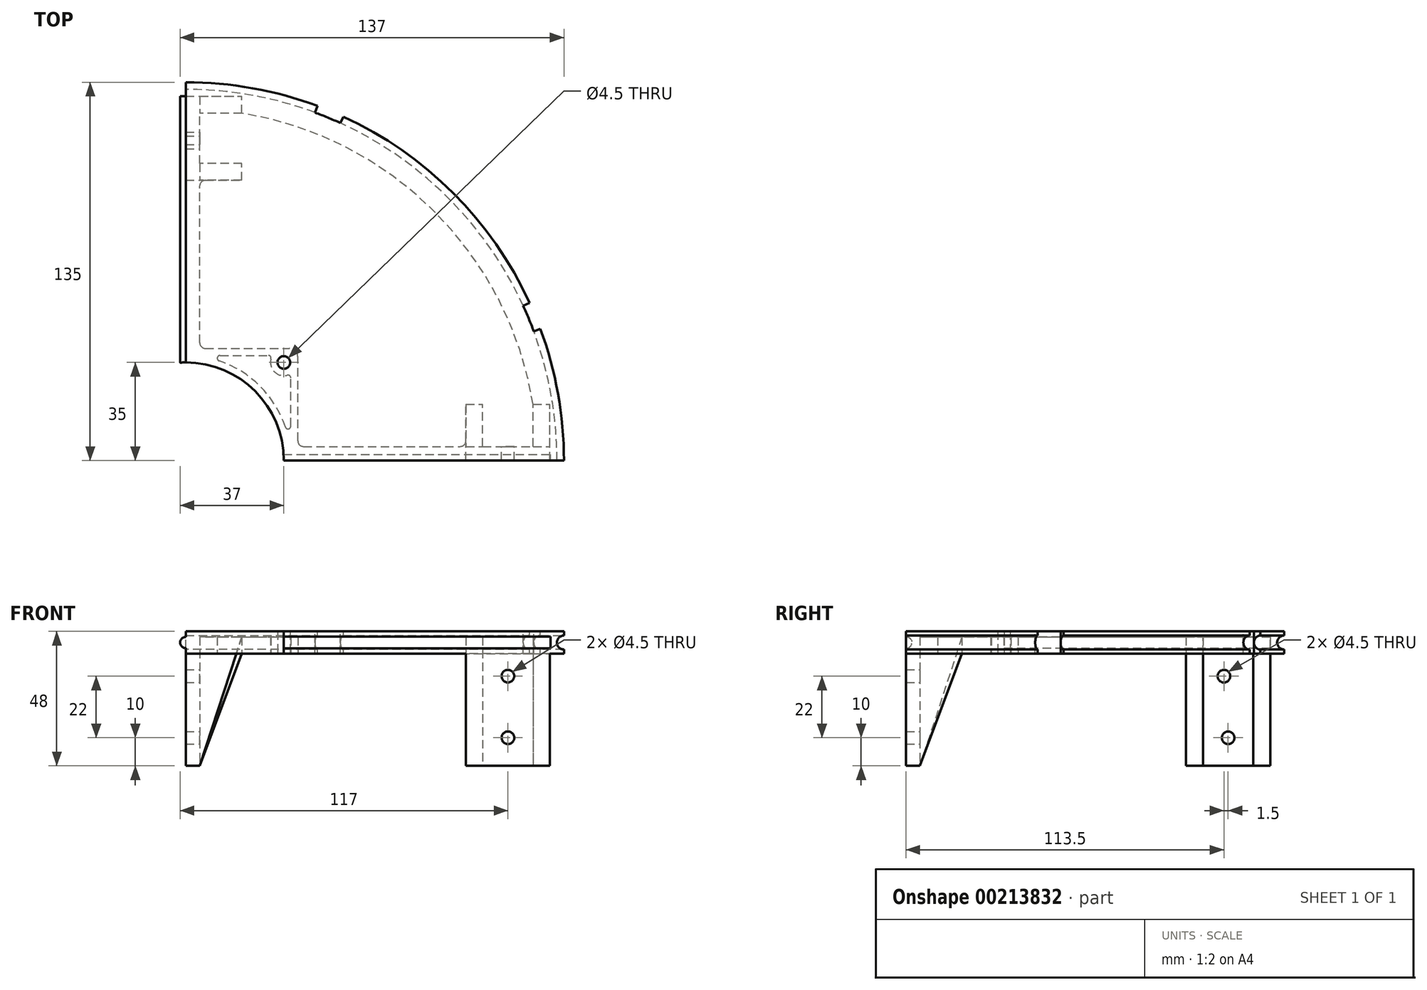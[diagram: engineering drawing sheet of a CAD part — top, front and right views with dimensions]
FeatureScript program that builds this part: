
annotation { "Feature Type Name" : "Feature", "Feature Type Description" : "" }
export const myFeature = defineFeature(function(context is Context, id is Id, definition is map)
    precondition{}
    {
        {
            var Q0;
            Q0=qCreatedBy(makeId("Top.planeOp"),FACE);
            var sketch = newSketch(context, id + "F0", { "sketchPlane" : qUnion([Q0])});
            skArc(sketch, "E0", {"start": v(135, 0) * mm, "mid": v(95.46, 95.46) * mm, "end": v(0, 135) * mm});
            skArc(sketch, "E1", {"start": v(35, 0) * mm, "mid": v(24.75, 24.75) * mm, "end": v(0, 35) * mm});
            skLineSegment(sketch, "E2.trimOffspring", {"start": v(35, 0) * mm, "end": v(135, 0) * mm});
            skLineSegment(sketch, "E3.1.5", {"start": v(0, 35) * mm, "end": v(0, 135) * mm});
            skCircle(sketch, "E4", {"center": v(35, 35) * mm, "radius": 2.25 * mm});
            skSolve(sketch);
        }
        {
            var Q0;
            Q0=qSketchRegion(id+"F0",true);
            extrude(context, id + "F1", {"entities" : qUnion([Q0]), "depth" : 8 * mm});
        }
        {
            var Q0;
            Q0=qCreatedBy(makeId("Top.planeOp"),FACE);
            cPlane(context, id + "F2", {"entities" : qUnion([Q0]), "cplaneType" : CPlaneType.OFFSET, "offset" : 4 * mm, "width" : 150 * mm, "height" : 150 * mm});
        }
        {
            var Q0;
            Q0=qCreatedBy(id+"F2.planeOp",FACE);
            var sketch = newSketch(context, id + "F3", { "sketchPlane" : qUnion([Q0])});
            skCircle(sketch, "E5", {"center": v(0, 0) * mm, "radius": 135 * mm});
            skSolve(sketch);
        }
        {
            var Q0;
            Q0=makeQuery(id+"F1.opExtrude","SWEPT_FACE",FACE,{"disambiguationData":[OSD([sQuery(id+"F0.wireOp",EDGE,"E2.trimOffspring")])]});
            var sketch = newSketch(context, id + "F4", { "sketchPlane" : qUnion([Q0])});
            skCircle(sketch, "E6", {"center": v(135, 4) * mm, "radius": 2.5 * mm});
            skSolve(sketch);
        }
        {
            var Q0;
            Q0=qSketchRegion(id+"F4",true);
            var Q1;
            Q1=qConstructionFilter(qBodyType(qCreatedBy(id+"F3",EDGE),BodyType.WIRE),ConstructionObject.NO);
            sweep(context, id + "F5", {"operationType" : NewBodyOperationType.REMOVE, "profiles" : qUnion([Q0]), "path" : qUnion([Q1])});
        }
        {
            var Q0;
            Q0=makeQuery(id+"F1.opExtrude","CAP_FACE",FACE,{"disambiguationData":[OSD([sQuery(id+"F0.wireOp",EDGE,"E0"),sQuery(id+"F0.wireOp",EDGE,"E1"),sQuery(id+"F0.wireOp",EDGE,"E2.trimOffspring"),sQuery(id+"F0.wireOp",EDGE,"E3.1.5"),sQuery(id+"F0.wireOp",EDGE,"E4")])],"isStart":true});
            var sketch = newSketch(context, id + "F6", { "sketchPlane" : qUnion([Q0])});
            skLineSegment(sketch, "E7.bottom", {"start": v(100, 0) * mm, "end": v(130, 0) * mm});
            skLineSegment(sketch, "E7.top", {"start": v(100, -20) * mm, "end": v(130, -20) * mm});
            skLineSegment(sketch, "E7.left", {"start": v(100, 0) * mm, "end": v(100, -20) * mm});
            skLineSegment(sketch, "E7.right", {"start": v(130, 0) * mm, "end": v(130, -20) * mm});
            skLineSegment(sketch, "E8.bottom", {"start": v(0, -100) * mm, "end": v(20, -100) * mm});
            skLineSegment(sketch, "E8.top", {"start": v(0, -130) * mm, "end": v(20, -130) * mm});
            skLineSegment(sketch, "E8.left", {"start": v(0, -100) * mm, "end": v(0, -130) * mm});
            skLineSegment(sketch, "E8.right", {"start": v(20, -100) * mm, "end": v(20, -130) * mm});
            skSolve(sketch);
        }
        {
            var Q0;
            Q0=qSketchRegion(id+"F6",true);
            extrude(context, id + "F7", {"entities" : qUnion([Q0]), "operationType" : NewBodyOperationType.ADD, "depth" : 40 * mm});
        }
        {
            var Q0;
            Q0=makeQuery(id+"F7.opExtrude","CAP_FACE",FACE,{"disambiguationData":[OSD([sQuery(id+"F6.wireOp",EDGE,"E7.bottom"),sQuery(id+"F6.wireOp",EDGE,"E7.top"),sQuery(id+"F6.wireOp",EDGE,"E7.left"),sQuery(id+"F6.wireOp",EDGE,"E7.right")])],"isStart":false});
            var sketch = newSketch(context, id + "F8", { "sketchPlane" : qUnion([Q0])});
            skLineSegment(sketch, "E9.bottom", {"start": v(106, -5) * mm, "end": v(124, -5) * mm});
            skLineSegment(sketch, "E9.top", {"start": v(106, -20) * mm, "end": v(124, -20) * mm});
            skLineSegment(sketch, "E9.left", {"start": v(106, -5) * mm, "end": v(106, -20) * mm});
            skLineSegment(sketch, "E9.right", {"start": v(124, -5) * mm, "end": v(124, -20) * mm});
            skLineSegment(sketch, "E10.bottom", {"start": v(20, -106) * mm, "end": v(5, -106) * mm});
            skLineSegment(sketch, "E10.top", {"start": v(20, -124) * mm, "end": v(5, -124) * mm});
            skLineSegment(sketch, "E10.left", {"start": v(20, -106) * mm, "end": v(20, -124) * mm});
            skLineSegment(sketch, "E10.right", {"start": v(5, -106) * mm, "end": v(5, -124) * mm});
            skSolve(sketch);
        }
        {
            var Q0;
            Q0=qSketchRegion(id+"F8",true);
            extrude(context, id + "F9", {"entities" : qUnion([Q0]), "operationType" : NewBodyOperationType.REMOVE, "oppositeDirection" : true, "depth" : 40 * mm});
        }
        {
            var Q0;
            {var subQ0=sQuery(id+"F6.wireOp",EDGE,"E7.right");var subQ1=sQuery(id+"F6.wireOp",EDGE,"E7.top");Q0=makeQuery(id+"F9.boolean.opBoolean","SPLIT",EDGE,{"disambiguationData":[TD([makeQuery(id+"F7.opExtrude","SWEPT_FACE",FACE,{"disambiguationData":[OSD([subQ0])]})])],"derivedFrom":makeQuery(id+"F7.opExtrude","CAP_EDGE",EDGE,{"disambiguationData":[OSD([subQ1])],"isStart":false})});}
            chamfer(context, id + "F10", {"entities" : qUnion([Q0]), "chamferType" : ChamferType.TWO_OFFSETS, "width1" : 15 * mm, "oppositeDirection" : false, "width2" : 40 * mm, "tangentPropagation" : true});
        }
        {
            var Q0;
            Q0=makeQuery(id+"F9.boolean.opBoolean","COPY",FACE,{"derivedFrom":makeQuery(id+"F9.opExtrude","SWEPT_FACE",FACE,{"disambiguationData":[OSD([sQuery(id+"F8.wireOp",EDGE,"E9.bottom")])]})});
            var sketch = newSketch(context, id + "F11", { "sketchPlane" : qUnion([Q0])});
            skCircle(sketch, "E11", {"center": v(-115, -8) * mm, "radius": 2.25 * mm});
            skCircle(sketch, "E12", {"center": v(-115, -30) * mm, "radius": 2.25 * mm});
            skSolve(sketch);
        }
        {
            var Q0;
            Q0=qSketchRegion(id+"F11",true);
            extrude(context, id + "F12", {"entities" : qUnion([Q0]), "operationType" : NewBodyOperationType.REMOVE, "oppositeDirection" : true, "depth" : 25 * mm});
        }
        {
            var Q0;
            {var subQ0=sQuery(id+"F6.wireOp",EDGE,"E8.right");var subQ1=sQuery(id+"F6.wireOp",EDGE,"E8.top");Q0=makeQuery(id+"F9.boolean.opBoolean","SPLIT",EDGE,{"disambiguationData":[TD([makeQuery(id+"F7.opExtrude","SWEPT_FACE",FACE,{"disambiguationData":[OSD([subQ1])]})])],"derivedFrom":makeQuery(id+"F7.opExtrude","CAP_EDGE",EDGE,{"disambiguationData":[OSD([subQ0])],"isStart":false})});}
            chamfer(context, id + "F13", {"entities" : qUnion([Q0]), "chamferType" : ChamferType.TWO_OFFSETS, "width1" : 40 * mm, "oppositeDirection" : false, "width2" : 15 * mm, "tangentPropagation" : true});
        }
        {
            var Q0;
            Q0=makeQuery(id+"F9.boolean.opBoolean","COPY",FACE,{"derivedFrom":makeQuery(id+"F9.opExtrude","SWEPT_FACE",FACE,{"disambiguationData":[OSD([sQuery(id+"F8.wireOp",EDGE,"E10.right")])]})});
            var sketch = newSketch(context, id + "F14", { "sketchPlane" : qUnion([Q0])});
            skCircle(sketch, "E13", {"center": v(115, -30) * mm, "radius": 2.25 * mm});
            skCircle(sketch, "E14", {"center": v(113.5, -8) * mm, "radius": 2.25 * mm});
            skSolve(sketch);
        }
        {
            var Q0;
            Q0=qSketchRegion(id+"F14",true);
            extrude(context, id + "F15", {"entities" : qUnion([Q0]), "operationType" : NewBodyOperationType.REMOVE, "oppositeDirection" : true, "depth" : 25 * mm});
        }
        {
            var Q0;
            Q0=makeQuery(id+"F1.opExtrude","CAP_FACE",FACE,{"disambiguationData":[OSD([sQuery(id+"F0.wireOp",EDGE,"E0"),sQuery(id+"F0.wireOp",EDGE,"E1"),sQuery(id+"F0.wireOp",EDGE,"E2.trimOffspring"),sQuery(id+"F0.wireOp",EDGE,"E3.1.5"),sQuery(id+"F0.wireOp",EDGE,"E4")])],"isStart":false});
            var sketch = newSketch(context, id + "F16", { "sketchPlane" : qUnion([Q0])});
            skArc(sketch, "E15", {"start": v(124.2, 46.14) * mm, "mid": v(122.41, 50.71) * mm, "end": v(120.45, 55.2) * mm});
            skArc(sketch, "E16", {"start": v(126.55, 47.01) * mm, "mid": v(124.72, 51.67) * mm, "end": v(122.72, 56.25) * mm});
            skLineSegment(sketch, "E17", {"start": v(0, 0) * mm, "end": v(124.72, 51.66) * mm, "construction": true});
            skLineSegment(sketch, "E18", {"start": v(0, 0) * mm, "end": v(51.66, 124.72) * mm, "construction": true});
            skLineSegment(sketch, "E19", {"start": v(46.13, 124.21) * mm, "end": v(47, 126.55) * mm});
            skLineSegment(sketch, "E20", {"start": v(124.2, 46.14) * mm, "end": v(126.55, 47.01) * mm});
            skLineSegment(sketch, "E21", {"start": v(55.2, 120.45) * mm, "end": v(56.24, 122.73) * mm});
            skLineSegment(sketch, "E22", {"start": v(120.45, 55.2) * mm, "end": v(122.72, 56.25) * mm});
            skArc(sketch, "E23.trimOffspring", {"start": v(56.24, 122.73) * mm, "mid": v(51.66, 124.73) * mm, "end": v(47, 126.55) * mm});
            skArc(sketch, "E24.trimOffspring", {"start": v(55.2, 120.45) * mm, "mid": v(50.7, 122.42) * mm, "end": v(46.13, 124.21) * mm});
            skSolve(sketch);
        }
        {
            var Q0;
            Q0=qSketchRegion(id+"F16",true);
            extrude(context, id + "F17", {"entities" : qUnion([Q0]), "operationType" : NewBodyOperationType.REMOVE, "oppositeDirection" : true, "depth" : 25 * mm});
        }
        {
            var Q0;
            Q0=makeQuery(id+"F7.boolean.opBoolean","MERGE",FACE,{"derivedFrom":[makeQuery(id+"F1.opExtrude","SWEPT_FACE",FACE,{"disambiguationData":[OSD([sQuery(id+"F0.wireOp",EDGE,"E2.trimOffspring")])]}),makeQuery(id+"F7.opExtrude","SWEPT_FACE",FACE,{"disambiguationData":[OSD([sQuery(id+"F6.wireOp",EDGE,"E7.bottom")])]})]});
            var sketch = newSketch(context, id + "F18", { "sketchPlane" : qUnion([Q0])});
            skLineSegment(sketch, "E25", {"start": v(0, 4) * mm, "end": v(130.2, 4) * mm});
            skSolve(sketch);
        }
        {
            var Q0;
            Q0=makeQuery(id+"F7.boolean.opBoolean","MERGE",FACE,{"derivedFrom":[makeQuery(id+"F1.opExtrude","SWEPT_FACE",FACE,{"disambiguationData":[OSD([sQuery(id+"F0.wireOp",EDGE,"E3.1.5")])]}),makeQuery(id+"F7.opExtrude","SWEPT_FACE",FACE,{"disambiguationData":[OSD([sQuery(id+"F6.wireOp",EDGE,"E8.left")])]})]});
            var sketch = newSketch(context, id + "F19", { "sketchPlane" : qUnion([Q0])});
            skLineSegment(sketch, "E26", {"start": v(-130, 4) * mm, "end": v(0, 4) * mm});
            skSolve(sketch);
        }
        {
            var Q0;
            Q0=qCreatedBy(makeId("Front.planeOp"),FACE);
            var sketch = newSketch(context, id + "F20", { "sketchPlane" : qUnion([Q0])});
            skCircle(sketch, "E27", {"center": v(0, 4) * mm, "radius": 2 * mm});
            skSolve(sketch);
        }
        {
            var Q0;
            Q0=makeQuery(id+"F20.imprint","IMPRINT",FACE,{"disambiguationData":[TD([[makeQuery(id+"F20.imprint","IMPRINT",EDGE,{"derivedFrom":sQuery(id+"F20.wireOp",EDGE,"E27")}),1.0]])]});
            var Q1;
            Q1=sQuery(id+"F19.wireOp",EDGE,"E26");
            sweep(context, id + "F21", {"operationType" : NewBodyOperationType.ADD, "profiles" : qUnion([Q0]), "path" : qUnion([Q1])});
        }
        {
            var Q0;
            Q0=makeQuery(id+"F1.opExtrude","CAP_FACE",FACE,{"disambiguationData":[OSD([sQuery(id+"F0.wireOp",EDGE,"E0"),sQuery(id+"F0.wireOp",EDGE,"E1"),sQuery(id+"F0.wireOp",EDGE,"E2.trimOffspring"),sQuery(id+"F0.wireOp",EDGE,"E3.1.5"),sQuery(id+"F0.wireOp",EDGE,"E4")])],"isStart":false});
            var sketch = newSketch(context, id + "F22", { "sketchPlane" : qUnion([Q0])});
            skCircle(sketch, "E28", {"center": v(0, 0) * mm, "radius": 35 * mm});
            skSolve(sketch);
        }
        {
            var Q0;
            {var subQ0=sQuery(id+"F22.wireOp",EDGE,"E28");var subQ1=makeQuery(id+"F22.imprint","INTERSECT",VERTEX,{"derivedFrom":[makeQuery(id+"F1.opExtrude","CAP_EDGE",EDGE,{"disambiguationData":[OSD([sQuery(id+"F0.wireOp",EDGE,"E2.trimOffspring")])],"isStart":false}),subQ0]});Q0=makeQuery(id+"F22.imprint","IMPRINT",FACE,{"disambiguationData":[TD([[makeQuery(id+"F22.imprint","IMPRINT",EDGE,{"disambiguationData":[TD([[subQ1,-1.0]])],"derivedFrom":subQ0}),1.0]])]});}
            extrude(context, id + "F23", {"entities" : qUnion([Q0]), "operationType" : NewBodyOperationType.REMOVE, "endBound" : BoundingType.THROUGH_ALL, "oppositeDirection" : true, "depth" : 25 * mm});
        }
        {
            var Q0;
            Q0=qCreatedBy(makeId("Right.planeOp"),FACE);
            var sketch = newSketch(context, id + "F24", { "sketchPlane" : qUnion([Q0])});
            skCircle(sketch, "E29", {"center": v(0, 4) * mm, "radius": 2.1 * mm});
            skSolve(sketch);
        }
        {
            var Q0;
            Q0=makeQuery(id+"F24.imprint","IMPRINT",FACE,{"disambiguationData":[TD([[makeQuery(id+"F24.imprint","IMPRINT",EDGE,{"derivedFrom":sQuery(id+"F24.wireOp",EDGE,"E29")}),1.0]])]});
            var Q1;
            Q1=sQuery(id+"F18.wireOp",EDGE,"E25");
            sweep(context, id + "F25", {"operationType" : NewBodyOperationType.REMOVE, "profiles" : qUnion([Q0]), "path" : qUnion([Q1])});
        }
        {
            var Q0;
            Q0=makeQuery(id+"F9.boolean.opBoolean","MERGE",FACE,{"derivedFrom":[makeQuery(id+"F1.opExtrude","CAP_FACE",FACE,{"disambiguationData":[OSD([sQuery(id+"F0.wireOp",EDGE,"E0"),sQuery(id+"F0.wireOp",EDGE,"E1"),sQuery(id+"F0.wireOp",EDGE,"E2.trimOffspring"),sQuery(id+"F0.wireOp",EDGE,"E3.1.5"),sQuery(id+"F0.wireOp",EDGE,"E4")])],"isStart":true}),makeQuery(id+"F9.opExtrude","CAP_FACE",FACE,{"disambiguationData":[OSD([sQuery(id+"F8.wireOp",EDGE,"E9.bottom"),sQuery(id+"F8.wireOp",EDGE,"E9.top"),sQuery(id+"F8.wireOp",EDGE,"E9.left"),sQuery(id+"F8.wireOp",EDGE,"E9.right")])],"isStart":false}),makeQuery(id+"F9.opExtrude","CAP_FACE",FACE,{"disambiguationData":[OSD([sQuery(id+"F8.wireOp",EDGE,"E10.bottom"),sQuery(id+"F8.wireOp",EDGE,"E10.top"),sQuery(id+"F8.wireOp",EDGE,"E10.left"),sQuery(id+"F8.wireOp",EDGE,"E10.right")])],"isStart":false})]});
            var sketch = newSketch(context, id + "F26", { "sketchPlane" : qUnion([Q0])});
            skLineSegment(sketch, "E30.top", {"start": v(7, -40) * mm, "end": v(37, -40) * mm});
            skLineSegment(sketch, "E30.right", {"start": v(40, -7) * mm, "end": v(40, -37) * mm});
            skArc(sketch, "E31", {"start": v(20, -124) * mm, "mid": v(88.81, -88.81) * mm, "end": v(124, -20) * mm});
            skLineSegment(sketch, "E32", {"start": v(106, -20) * mm, "end": v(100, -20) * mm});
            skLineSegment(sketch, "E33", {"start": v(5, -42) * mm, "end": v(5, -100) * mm});
            skLineSegment(sketch, "E34", {"start": v(42, -5) * mm, "end": v(100, -5) * mm});
            skLineSegment(sketch, "E35", {"start": v(100, -5) * mm, "end": v(100, -20) * mm});
            skPoint(sketch, "E36.visualSharp", {"position": v(40, -40) * mm});
            skArc(sketch, "E36.filletArc", {"start": v(37, -40) * mm, "mid": v(39.12, -39.12) * mm, "end": v(40, -37) * mm});
            skArc(sketch, "E37.filletArc", {"start": v(7, -40) * mm, "mid": v(5.59, -40.59) * mm, "end": v(5, -42) * mm});
            skArc(sketch, "E38.filletArc", {"start": v(42, -5) * mm, "mid": v(40.59, -5.59) * mm, "end": v(40, -7) * mm});
            skLineSegment(sketch, "E39.bottom", {"start": v(5, -124) * mm, "end": v(20, -124) * mm});
            skLineSegment(sketch, "E39.left", {"start": v(5, -124) * mm, "end": v(5, -106) * mm});
            skLineSegment(sketch, "E40.left", {"start": v(106, -5) * mm, "end": v(106, -20) * mm});
            skLineSegment(sketch, "E40.right", {"start": v(124, -5) * mm, "end": v(124, -20) * mm});
            skLineSegment(sketch, "E41", {"start": v(106, -5) * mm, "end": v(124, -5) * mm});
            skLineSegment(sketch, "E42", {"start": v(5, -106) * mm, "end": v(20, -106) * mm});
            skLineSegment(sketch, "E43", {"start": v(20, -106) * mm, "end": v(20, -100) * mm});
            skLineSegment(sketch, "E44", {"start": v(20, -100) * mm, "end": v(5, -100) * mm});
            skSolve(sketch);
        }
        {
            var Q0;
            Q0=qSketchRegion(id+"F26",true);
            extrude(context, id + "F27", {"entities" : qUnion([Q0]), "operationType" : NewBodyOperationType.REMOVE, "oppositeDirection" : true, "depth" : 6 * mm});
        }
        {
            var Q0;
            {var subQ0=sQuery(id+"F0.wireOp",EDGE,"E1");var subQ1=sQuery(id+"F0.wireOp",EDGE,"E2.trimOffspring");var subQ2=sQuery(id+"F0.wireOp",EDGE,"E3.1.5");var subQ3=sQuery(id+"F0.wireOp",EDGE,"E4");Q0=makeQuery(id+"F27.boolean.opBoolean","SPLIT",FACE,{"disambiguationData":[TD([makeQuery(id+"F1.opExtrude","SWEPT_FACE",FACE,{"disambiguationData":[OSD([subQ0])]})])],"derivedFrom":makeQuery(id+"F9.boolean.opBoolean","MERGE",FACE,{"derivedFrom":[makeQuery(id+"F1.opExtrude","CAP_FACE",FACE,{"disambiguationData":[OSD([sQuery(id+"F0.wireOp",EDGE,"E0"),subQ0,subQ1,subQ2,subQ3])],"isStart":true}),makeQuery(id+"F9.opExtrude","CAP_FACE",FACE,{"disambiguationData":[OSD([sQuery(id+"F8.wireOp",EDGE,"E9.bottom"),sQuery(id+"F8.wireOp",EDGE,"E9.top"),sQuery(id+"F8.wireOp",EDGE,"E9.left"),sQuery(id+"F8.wireOp",EDGE,"E9.right")])],"isStart":false}),makeQuery(id+"F9.opExtrude","CAP_FACE",FACE,{"disambiguationData":[OSD([sQuery(id+"F8.wireOp",EDGE,"E10.bottom"),sQuery(id+"F8.wireOp",EDGE,"E10.top"),sQuery(id+"F8.wireOp",EDGE,"E10.left"),sQuery(id+"F8.wireOp",EDGE,"E10.right")])],"isStart":false})]})});}
            var sketch = newSketch(context, id + "F28", { "sketchPlane" : qUnion([Q0])});
            skArc(sketch, "E45", {"start": v(11.93, -35.55) * mm, "mid": v(26.52, -26.52) * mm, "end": v(35.55, -11.93) * mm});
            skLineSegment(sketch, "E46.top", {"start": v(12.25, -37.5) * mm, "end": v(29.45, -37.5) * mm});
            skLineSegment(sketch, "E46.right", {"start": v(37.5, -12.25) * mm, "end": v(37.5, -29.45) * mm});
            skArc(sketch, "E47", {"start": v(36.24, -30.41) * mm, "mid": v(31.64, -31.64) * mm, "end": v(30.41, -36.24) * mm});
            skPoint(sketch, "E48.visualSharp", {"position": v(0, -37.5) * mm});
            skArc(sketch, "E48.filletArc", {"start": v(11.93, -35.55) * mm, "mid": v(11.26, -36.66) * mm, "end": v(12.25, -37.5) * mm});
            skPoint(sketch, "E49.visualSharp", {"position": v(37.5, 0) * mm});
            skArc(sketch, "E49.filletArc", {"start": v(37.5, -12.25) * mm, "mid": v(36.66, -11.26) * mm, "end": v(35.55, -11.93) * mm});
            skPoint(sketch, "E50.visualSharp", {"position": v(30.96, -37.5) * mm});
            skArc(sketch, "E50.filletArc", {"start": v(29.45, -37.5) * mm, "mid": v(30.24, -37.1) * mm, "end": v(30.41, -36.24) * mm});
            skPoint(sketch, "E51.visualSharp", {"position": v(37.5, -30.96) * mm});
            skArc(sketch, "E51.filletArc", {"start": v(36.24, -30.41) * mm, "mid": v(37.1, -30.24) * mm, "end": v(37.5, -29.45) * mm});
            skSolve(sketch);
        }
        {
            var Q0;
            Q0=makeQuery(id+"F28.imprint","IMPRINT",FACE,{"disambiguationData":[TD([[makeQuery(id+"F28.imprint","IMPRINT",EDGE,{"derivedFrom":sQuery(id+"F28.wireOp",EDGE,"E45")}),-1.0]])]});
            extrude(context, id + "F29", {"entities" : qUnion([Q0]), "operationType" : NewBodyOperationType.REMOVE, "oppositeDirection" : true, "depth" : 6 * mm});
        }
        {
            var Q0;
            {var subQ0=sQuery(id+"F6.wireOp",EDGE,"E8.bottom");var subQ1=sQuery(id+"F6.wireOp",EDGE,"E8.right");Q0=makeQuery(id+"F9.boolean.opBoolean","SPLIT",EDGE,{"disambiguationData":[TD([makeQuery(id+"F7.opExtrude","SWEPT_FACE",FACE,{"disambiguationData":[OSD([subQ0])]})])],"derivedFrom":makeQuery(id+"F7.opExtrude","CAP_EDGE",EDGE,{"disambiguationData":[OSD([subQ1])],"isStart":false})});}
            chamfer(context, id + "F30", {"entities" : qUnion([Q0]), "chamferType" : ChamferType.TWO_OFFSETS, "width1" : 46 * mm, "oppositeDirection" : false, "width2" : 15 * mm, "tangentPropagation" : true});
        }
        {
            var Q0;
            {var subQ0=sQuery(id+"F6.wireOp",EDGE,"E7.left");var subQ1=sQuery(id+"F6.wireOp",EDGE,"E7.top");Q0=makeQuery(id+"F9.boolean.opBoolean","SPLIT",EDGE,{"disambiguationData":[TD([makeQuery(id+"F7.opExtrude","SWEPT_FACE",FACE,{"disambiguationData":[OSD([subQ0])]})])],"derivedFrom":makeQuery(id+"F7.opExtrude","CAP_EDGE",EDGE,{"disambiguationData":[OSD([subQ1])],"isStart":false})});}
            chamfer(context, id + "F31", {"entities" : qUnion([Q0]), "chamferType" : ChamferType.TWO_OFFSETS, "width1" : 15 * mm, "oppositeDirection" : false, "width2" : 46 * mm, "tangentPropagation" : true});
        }
        {
            var Q0;
            Q0=makeQuery(id+"F27.boolean.opBoolean","COPY",EDGE,{"derivedFrom":makeQuery(id+"F27.opExtrude","SWEPT_EDGE",EDGE,{"disambiguationData":[OSD([sQuery(id+"F6.wireOp",EDGE,"E8.bottom"),sQuery(id+"F26.wireOp",EDGE,"E33"),sQuery(id+"F26.wireOp",EDGE,"E44")])]})});
            var Q1;
            Q1=makeQuery(id+"F27.boolean.opBoolean","COPY",EDGE,{"derivedFrom":makeQuery(id+"F27.opExtrude","SWEPT_EDGE",EDGE,{"disambiguationData":[OSD([sQuery(id+"F6.wireOp",EDGE,"E7.left"),sQuery(id+"F26.wireOp",EDGE,"E34"),sQuery(id+"F26.wireOp",EDGE,"E35")])]})});
            fillet(context, id + "F32", {"entities" : qUnion([Q0, Q1]), "radius" : 2 * mm, "tangentPropagation" : true, "allowEdgeOverflow" : false});
        }
    });
